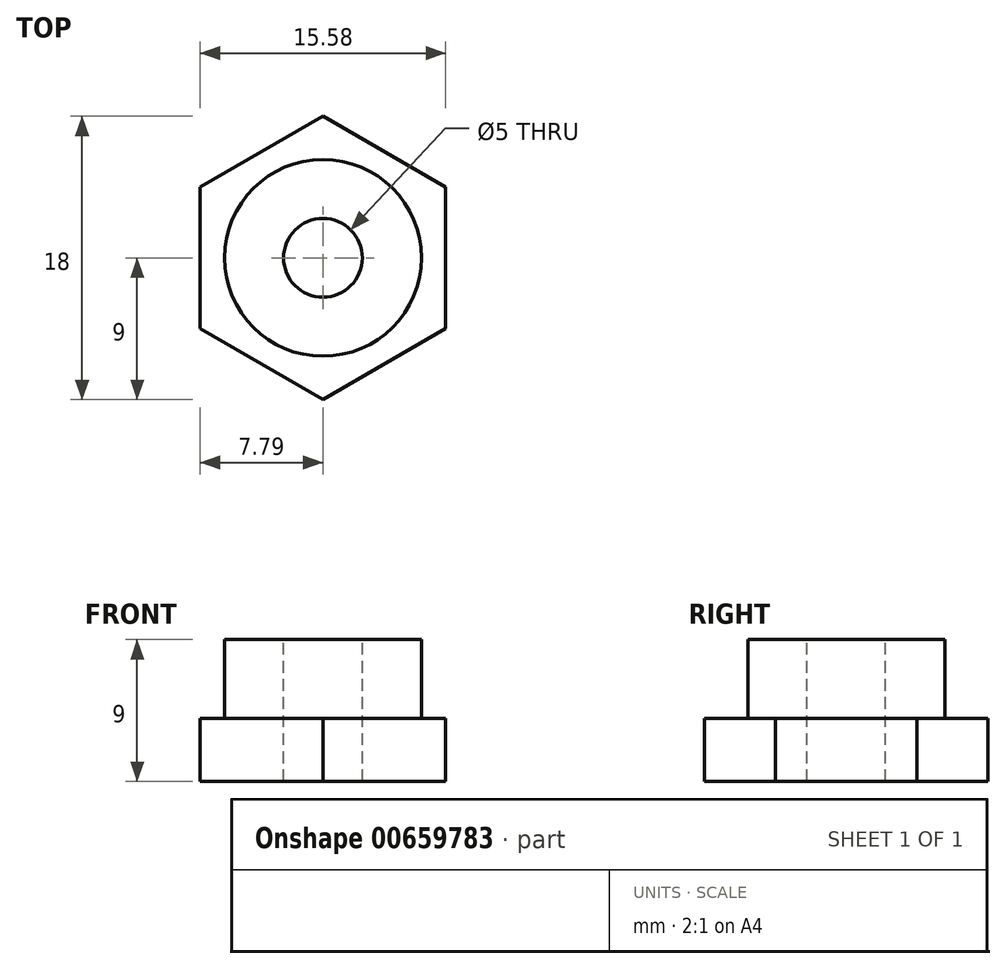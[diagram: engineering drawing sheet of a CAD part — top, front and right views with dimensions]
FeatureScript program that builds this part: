
annotation { "Feature Type Name" : "Feature", "Feature Type Description" : "" }
export const myFeature = defineFeature(function(context is Context, id is Id, definition is map)
    precondition{}
    {
        {
            var Q0;
            Q0=qCreatedBy(makeId("Top.planeOp"),FACE);
            var sketch = newSketch(context, id + "F0", { "sketchPlane" : qUnion([Q0])});
            skCircle(sketch, "E0.cCircle", {"center": v(0, 0) * mm, "radius": 7.8 * mm, "construction": true});
            skLineSegment(sketch, "E0.0", {"start": v(-7.8, -4.5) * mm, "end": v(-7.8, 4.5) * mm});
            skLineSegment(sketch, "E0.1", {"start": v(-7.8, 4.5) * mm, "end": v(0, 9) * mm});
            skLineSegment(sketch, "E0.2", {"start": v(0, 9) * mm, "end": v(7.8, 4.5) * mm});
            skLineSegment(sketch, "E0.3", {"start": v(7.8, 4.5) * mm, "end": v(7.8, -4.5) * mm});
            skLineSegment(sketch, "E0.4", {"start": v(7.8, -4.5) * mm, "end": v(0, -9) * mm});
            skLineSegment(sketch, "E0.5", {"start": v(0, -9) * mm, "end": v(-7.8, -4.5) * mm});
            skPoint(sketch, "E0.0.midPoint", {"position": v(-7.8, 0) * mm});
            skSolve(sketch);
        }
        {
            var Q0;
            Q0=qCreatedBy(makeId("Top.planeOp"),FACE);
            var sketch = newSketch(context, id + "F1", { "sketchPlane" : qUnion([Q0])});
            skCircle(sketch, "E1", {"center": v(0, 0) * mm, "radius": 6.25 * mm});
            skSolve(sketch);
        }
        {
            var Q0;
            Q0=makeQuery(id+"F0.imprint","IMPRINT",FACE,{"disambiguationData":[TD([[makeQuery(id+"F0.imprint","IMPRINT",EDGE,{"derivedFrom":sQuery(id+"F0.wireOp",EDGE,"E0.0")}),-1.0]])]});
            extrude(context, id + "F2", {"entities" : qUnion([Q0]), "depth" : 4 * mm, "offsetDistance" : 25 * mm});
        }
        {
            var Q0;
            Q0 = qSketchRegion(id + "F1", true);
            extrude(context, id + "F3", {"entities" : qUnion([Q0]), "operationType" : NewBodyOperationType.ADD, "depth" : 9 * mm, "offsetDistance" : 25 * mm});
        }
        {
            var Q0;
            Q0=makeQuery(id+"F3.opExtrude","CAP_FACE",FACE,{"disambiguationData":[OSD([sQuery(id+"F1.wireOp",EDGE,"E1")])],"isStart":false});
            var sketch = newSketch(context, id + "F4", { "sketchPlane" : qUnion([Q0])});
            skLineSegment(sketch, "E2", {"start": v(-0.55, 0) * mm, "end": v(0, 0) * mm});
            skSolve(sketch);
        }
        {
            var Q0;
            Q0=sQuery(id+"F4.wireOp",VERTEX,"E2.end");
            var Q1;
            Q1=makeQuery(id+"F2.opExtrude","SWEPT_BODY",BODY,{"disambiguationData":[OSD([sQuery(id+"F0.wireOp",EDGE,"E0.0"),sQuery(id+"F0.wireOp",EDGE,"E0.1"),sQuery(id+"F0.wireOp",EDGE,"E0.2"),sQuery(id+"F0.wireOp",EDGE,"E0.3"),sQuery(id+"F0.wireOp",EDGE,"E0.4"),sQuery(id+"F0.wireOp",EDGE,"E0.5")])]});
            hole(context, id + "F5", {"style" : HoleStyle.SIMPLE, "endStyle" : HoleEndStyle.THROUGH, "holeDiameter" : 5 * mm, "majorDiameter" : 5 * mm, "isTappedThrough" : true, "tappedDepth" : 12 * mm, "tapClearance" : 3, "locations" : qUnion([Q0]), "scope" : qUnion([Q1])});
        }
    });
